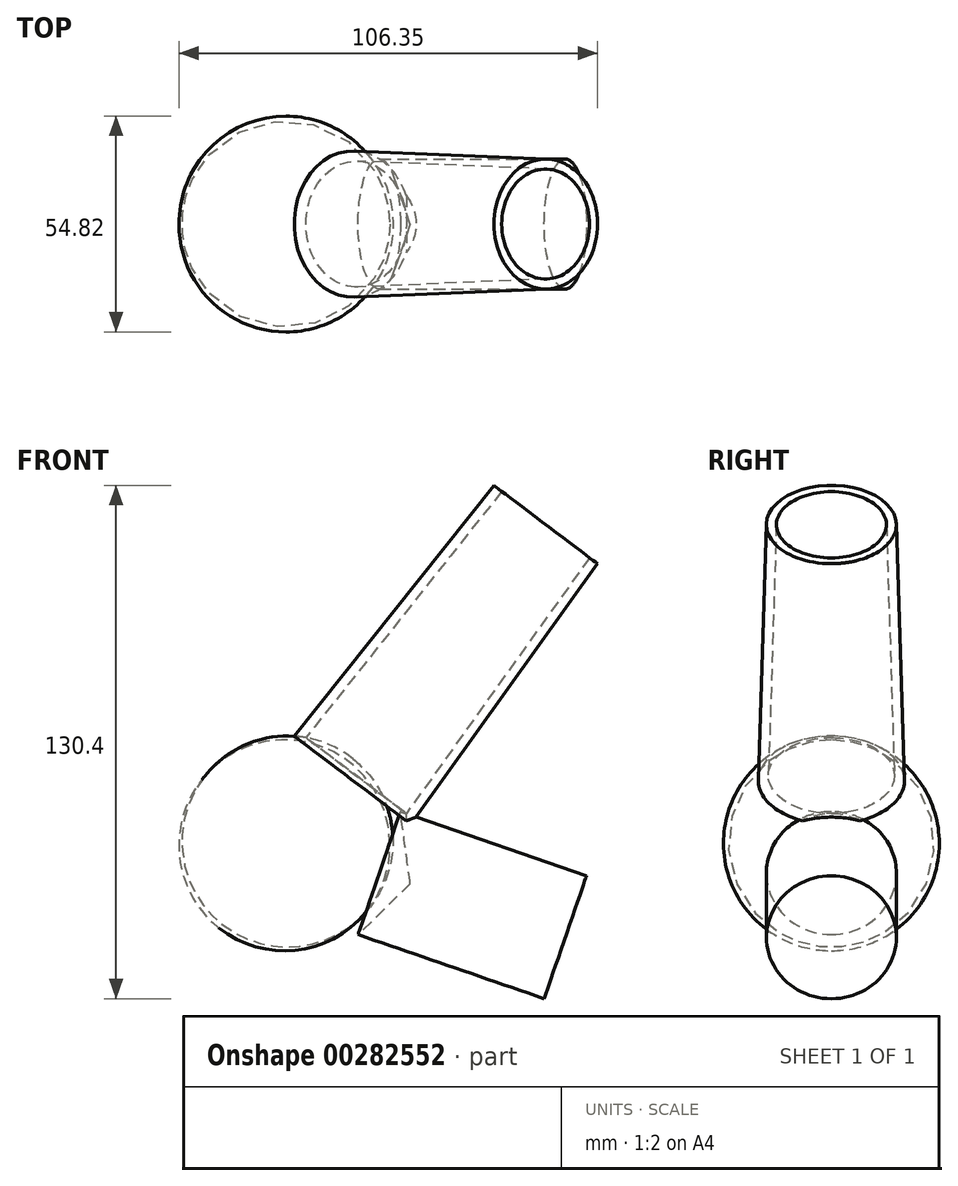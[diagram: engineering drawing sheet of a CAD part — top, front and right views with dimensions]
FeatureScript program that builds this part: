
annotation { "Feature Type Name" : "Feature", "Feature Type Description" : "" }
export const myFeature = defineFeature(function(context is Context, id is Id, definition is map)
    precondition{}
    {
        {
            var Q0;
            Q0=qCreatedBy(makeId("Front.planeOp"),FACE);
            var sketch = newSketch(context, id + "F0", { "sketchPlane" : qUnion([Q0])});
            skLineSegment(sketch, "E0", {"start": v(0, 11) * mm, "end": v(51.66, 75.95) * mm});
            skLineSegment(sketch, "E1", {"start": v(51.66, 75.95) * mm, "end": v(25.82, 96.51) * mm});
            skLineSegment(sketch, "E2", {"start": v(25.82, 96.51) * mm, "end": v(-25.85, 31.57) * mm});
            skCircle(sketch, "E3", {"center": v(-26.62, 6.04) * mm, "radius": 26.8 * mm});
            skLineSegment(sketch, "E4.bottom", {"start": v(0, 32.15) * mm, "end": v(-22.55, 32.15) * mm});
            skLineSegment(sketch, "E4.left", {"start": v(0, 32.15) * mm, "end": v(0, 7.8) * mm});
            skPoint(sketch, "E4.middle", {"position": v(-11.27, 19.98) * mm});
            skLineSegment(sketch, "E5", {"start": v(38.74, 86.23) * mm, "end": v(-11.27, 19.98) * mm});
            skLineSegment(sketch, "E6", {"start": v(-6.04, -11.12) * mm, "end": v(-47.96, 22.23) * mm});
            skLineSegment(sketch, "E7", {"start": v(-12.04, -16.44) * mm, "end": v(38.62, -33.9) * mm});
            skLineSegment(sketch, "E8", {"start": v(38.62, -33.9) * mm, "end": v(49.38, -2.67) * mm});
            skLineSegment(sketch, "E9", {"start": v(49.38, -2.67) * mm, "end": v(-1.29, 14.78) * mm});
            skLineSegment(sketch, "E10", {"start": v(44, -18.28) * mm, "end": v(-6.66, -0.83) * mm});
            skLineSegment(sketch, "E11", {"start": v(2.08, 13.62) * mm, "end": v(4.59, -4.7) * mm});
            skLineSegment(sketch, "E12", {"start": v(4.59, -4.7) * mm, "end": v(-9.24, -17.4) * mm});
            skSolve(sketch);
        }
        {
            var Q0;
            {var subQ5=sQuery(id+"F0.wireOp",EDGE,"E2");var subQ6=sQuery(id+"F0.wireOp",EDGE,"E1");var subQ7=makeQuery(id+"F0.imprint","INTERSECT",VERTEX,{"derivedFrom":[subQ6,subQ5]});Q0=makeQuery(id+"F0.imprint","IMPRINT",FACE,{"disambiguationData":[TD([[makeQuery(id+"F0.imprint","IMPRINT",EDGE,{"disambiguationData":[TD([[subQ7,1.0]])],"derivedFrom":subQ6}),1.0]])]});}
            var Q1;
            Q1=sQuery(id+"F0.wireOp",EDGE,"E5");
            revolve(context, id + "F1", {"entities" : qUnion([Q0]), "axis" : qUnion([Q1]), "revolveType" : RevolveType.FULL});
        }
        {
            var Q0;
            {var subQ0=sQuery(id+"F0.wireOp",EDGE,"E6");Q0=makeQuery(id+"F0.imprint","IMPRINT",FACE,{"disambiguationData":[TD([[makeQuery(id+"F0.imprint","IMPRINT",EDGE,{"derivedFrom":subQ0}),1.0]])]});}
            var Q1;
            Q1=sQuery(id+"F0.wireOp",EDGE,"E6");
            revolve(context, id + "F2", {"entities" : qUnion([Q0]), "axis" : qUnion([Q1]), "revolveType" : RevolveType.FULL});
        }
        {
            var Q0;
            Q0=makeQuery(id+"F1.opRevolve","SWEPT_FACE",FACE,{"disambiguationData":[OSD([sQuery(id+"F0.wireOp",EDGE,"E1")])]});
            var Q1;
            Q1=makeQuery(id+"F1.opRevolve","SWEPT_FACE",FACE,{"disambiguationData":[OSD([sQuery(id+"F0.wireOp",EDGE,"E3")])]});
            shell(context, id + "F3", {"entities" : qUnion([Q0, Q1]), "thickness" : 2.54 * mm});
        }
        {
            var Q0;
            {var subQ5=sQuery(id+"F0.wireOp",EDGE,"E11");Q0=makeQuery(id+"F0.imprint","IMPRINT",FACE,{"disambiguationData":[TD([[makeQuery(id+"F0.imprint","IMPRINT",EDGE,{"derivedFrom":subQ5}),1.0]])]});}
            var Q1;
            Q1=sQuery(id+"F0.wireOp",EDGE,"E10");
            revolve(context, id + "F4", {"operationType" : NewBodyOperationType.ADD, "entities" : qUnion([Q0]), "axis" : qUnion([Q1]), "revolveType" : RevolveType.FULL});
        }
    });
